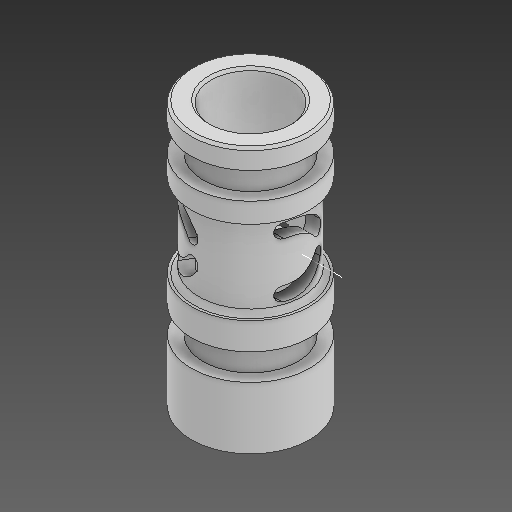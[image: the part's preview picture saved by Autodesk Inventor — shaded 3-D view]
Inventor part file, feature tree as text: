
AUTODESK INVENTOR PART (.ipt)
format: ipt  version: 2021 (Build 250183000, 183)  size: 477,696 bytes
history: native  units: mm
features: sketch x6, extrude x4, other x4, plane x3, chamfer x3, revolve x2, pattern_circular x2, fillet x1
ambient origin geometry x8: Origin, YZ Plane, XZ Plane, XY Plane, X Axis, Y Axis, Z Axis, Center Point
bodies: Solid1 (feature_tree)
feature tree (25):
  revolve  "Revolution1"  Angle=90.0deg
  plane  "Work Plane1"
  extrude  "Extrusion1"  Depth=2.0mm
  other  "Work Axis1"
  revolve  "Revolution2"  [1 undecoded]
  fillet  "Fillet1"  Radius=4.0mm
  pattern_circular  "Circular Pattern1"  Count=3 Angle=360.0deg
  plane  "Work Plane3"
  extrude  "Extrusion2"  Depth=2.5mm
  chamfer  "Chamfer3"  Angle=90.0deg  [1 undecoded]
  extrude  "Extrusion6"  Depth=0.1mm
  chamfer  "Chamfer5"  Distance=10.0mm
  other  "Work Axis2"
  chamfer  "Chamfer6"  Distance=0.25mm Angle=45.0deg
  plane  "Work Plane4"
  extrude  "Extrusion8"  Depth=9.0mm
  pattern_circular  "Circular Pattern3"  [2 undecoded]
  sketch  "Sketch2"  dims[d2=23.0mm d11=90.0deg]
  sketch  "Sketch3"  dims[d13=2.0mm d14=2.0mm]
  sketch  "Sketch4"  dims[d15=3.490659mm d16=3.490659mm d18=4.0mm]
  sketch  "Sketch5"  dims[d19=10.0mm d20=0.0mm]
  other  "Srf1"
  sketch  "Sketch10"  dims[d24=90.0deg]
  sketch  "Sketch13"  dims[d25=0.5mm d29=30.0mm d30=360.0deg d32=2.5mm d33=90.0deg d34=0.1mm d35=10.0mm d36=0.0mm d47=0.25mm d48=2.0mm d49=45.0deg d59=9.0mm d60=4.0mm d61=0.0mm d64=8.0mm d67=0.5mm d68=2.0mm d69=45.0deg d74=11.0mm d75=8.5mm d77=9.6mm d78=2.7mm d80=0.75mm d84=12.0mm d86=2.0mm d87=0.2mm d88=2.0mm d89=45.0deg d90=18.0mm d91=10.0mm d92=0.0mm d96=30.0mm d97=360.0deg d76=0.5mm d79=0.872665mm]
  other  "Unwrap1"
note: 4 required parameter values undecoded (feature->parameter linkage not recoverable at this tier; creation-order binding heuristic only, values carry confidence <= 0.55)